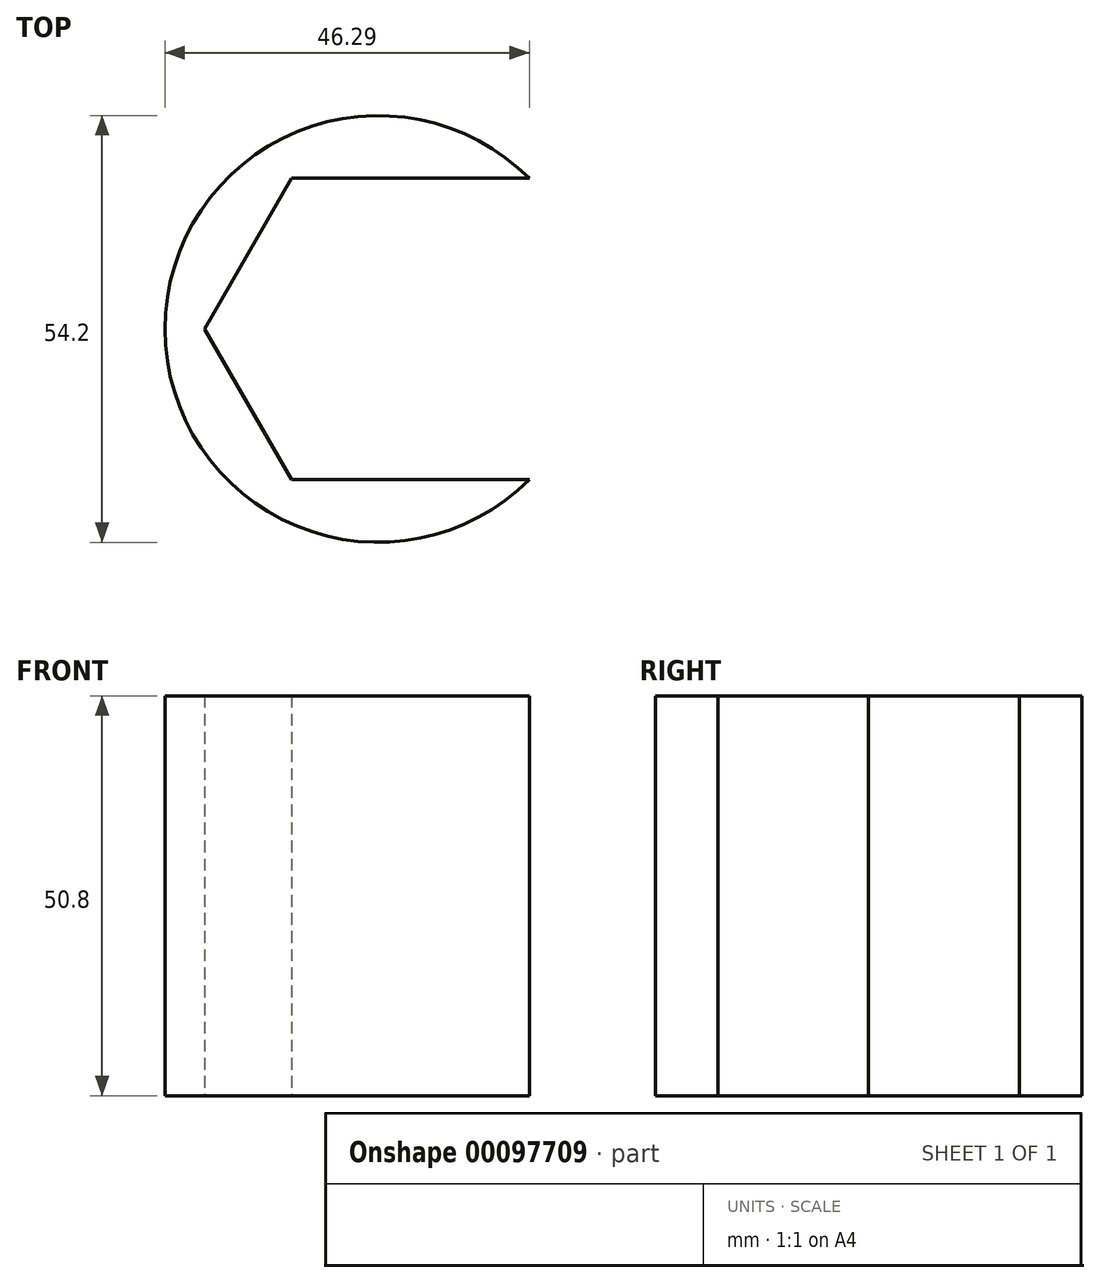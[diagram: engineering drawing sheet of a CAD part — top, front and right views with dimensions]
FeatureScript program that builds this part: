
annotation { "Feature Type Name" : "Feature", "Feature Type Description" : "" }
export const myFeature = defineFeature(function(context is Context, id is Id, definition is map)
    precondition{}
    {
        {
            var Q0;
            Q0=qCreatedBy(makeId("Top.planeOp"),FACE);
            var sketch = newSketch(context, id + "F0", { "sketchPlane" : qUnion([Q0])});
            skCircle(sketch, "E0", {"center": v(0, 0) * mm, "radius": 27.1 * mm});
            skCircle(sketch, "E1.cCircle", {"center": v(0, 0) * mm, "radius": 19.13 * mm, "construction": true});
            skLineSegment(sketch, "E1.0", {"start": v(22.1, 0) * mm, "end": v(11.05, -19.13) * mm});
            skLineSegment(sketch, "E1.1", {"start": v(11.05, -19.13) * mm, "end": v(-11.05, -19.13) * mm});
            skLineSegment(sketch, "E1.2", {"start": v(-11.05, -19.13) * mm, "end": v(-22.1, 0) * mm});
            skLineSegment(sketch, "E1.3", {"start": v(-22.1, 0) * mm, "end": v(-11.05, 19.13) * mm});
            skLineSegment(sketch, "E1.4", {"start": v(-11.05, 19.13) * mm, "end": v(11.05, 19.13) * mm});
            skLineSegment(sketch, "E1.5", {"start": v(11.05, 19.13) * mm, "end": v(22.1, 0) * mm});
            skPoint(sketch, "E1.0.midPoint", {"position": v(16.57, -9.57) * mm});
            skSolve(sketch);
        }
        {
            var Q0;
            Q0 = qSketchRegion(id + "F0", true);
            extrude(context, id + "F1", {"entities" : qUnion([Q0]), "depth" : 50.8 * mm});
        }
        {
            var Q0;
            Q0=makeQuery(id+"F1.opExtrude","CAP_FACE",FACE,{"disambiguationData":[OSD([sQuery(id+"F0.wireOp",EDGE,"E0"),sQuery(id+"F0.wireOp",EDGE,"E1.0"),sQuery(id+"F0.wireOp",EDGE,"E1.1"),sQuery(id+"F0.wireOp",EDGE,"E1.2"),sQuery(id+"F0.wireOp",EDGE,"E1.3"),sQuery(id+"F0.wireOp",EDGE,"E1.4"),sQuery(id+"F0.wireOp",EDGE,"E1.5")])],"isStart":false});
            var sketch = newSketch(context, id + "F2", { "sketchPlane" : qUnion([Q0])});
            skLineSegment(sketch, "E2.bottom", {"start": v(0, 19.13) * mm, "end": v(42.4, 19.13) * mm});
            skLineSegment(sketch, "E2.top", {"start": v(0, -19.13) * mm, "end": v(42.4, -19.13) * mm});
            skLineSegment(sketch, "E2.left", {"start": v(0, 19.13) * mm, "end": v(0, -19.13) * mm});
            skLineSegment(sketch, "E2.right", {"start": v(42.4, 19.13) * mm, "end": v(42.4, -19.13) * mm});
            skSolve(sketch);
        }
        {
            var Q0;
            Q0 = qSketchRegion(id + "F2", true);
            extrude(context, id + "F3", {"entities" : qUnion([Q0]), "operationType" : NewBodyOperationType.REMOVE, "oppositeDirection" : true, "depth" : 50.8 * mm});
        }
    });
